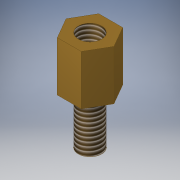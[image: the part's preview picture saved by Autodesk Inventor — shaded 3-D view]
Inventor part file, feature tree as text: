
AUTODESK INVENTOR PART (.ipt)
format: ipt  version: 2019 (Build 230136000, 136)  size: 120,832 bytes
history: native  units: mm
features: extrude x3, sketch x3, thread x2, other x1
ambient origin geometry x8: Origin, YZ Plane, XZ Plane, XY Plane, X Axis, Y Axis, Z Axis, Center Point
bodies: Body1 (feature_tree)
feature tree (9):
  other  "Твердое тело1"
  extrude  "Выдавливание1"  Depth=5.0mm
  extrude  "Выдавливание2"  Depth=6.0mm TaperAngle=0.0deg
  extrude  "Выдавливание3"  Depth=2.8mm
  thread  "Резьба1"
  thread  "Резьба2"
  sketch  "Эскиз1"
  sketch  "Эскиз2"
  sketch  "Эскиз3"
